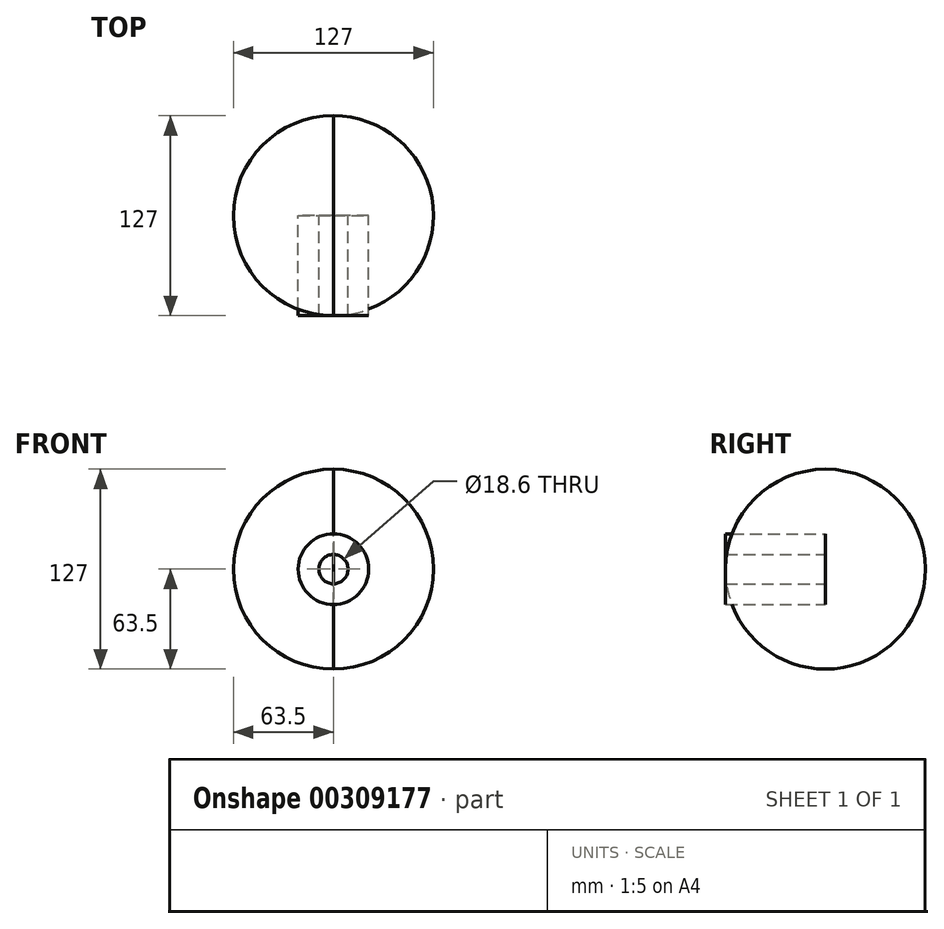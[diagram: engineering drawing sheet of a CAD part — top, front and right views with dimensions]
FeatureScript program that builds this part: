
annotation { "Feature Type Name" : "Feature", "Feature Type Description" : "" }
export const myFeature = defineFeature(function(context is Context, id is Id, definition is map)
    precondition{}
    {
        {
            var Q0;
            Q0=qCreatedBy(makeId("Top.planeOp"),FACE);
            var sketch = newSketch(context, id + "F0", { "sketchPlane" : qUnion([Q0])});
            skCircle(sketch, "E0", {"center": v(0, 0) * mm, "radius": 63.5 * mm});
            skLineSegment(sketch, "E1", {"start": v(0, 63.5) * mm, "end": v(0, -63.5) * mm});
            skSolve(sketch);
        }
        {
            var Q0;
            {var subQ0=sQuery(id+"F0.wireOp",EDGE,"E1");Q0=makeQuery(id+"F0.imprint","IMPRINT",FACE,{"disambiguationData":[TD([[makeQuery(id+"F0.imprint","IMPRINT",EDGE,{"derivedFrom":subQ0}),-1.0]])]});}
            var Q1;
            Q1=sQuery(id+"F0.wireOp",EDGE,"E1");
            revolve(context, id + "F1", {"entities" : qUnion([Q0]), "axis" : qUnion([Q1]), "revolveType" : RevolveType.SYMMETRIC, "angle" : 180 * degree});
        }
        {
            var Q0;
            {var subQ0=sQuery(id+"F0.wireOp",EDGE,"E1");Q0=makeQuery(id+"F0.imprint","IMPRINT",FACE,{"disambiguationData":[TD([[makeQuery(id+"F0.imprint","IMPRINT",EDGE,{"derivedFrom":subQ0}),1.0]])]});}
            var Q1;
            Q1=sQuery(id+"F0.wireOp",EDGE,"E1");
            revolve(context, id + "F2", {"entities" : qUnion([Q0]), "axis" : qUnion([Q1]), "revolveType" : RevolveType.SYMMETRIC, "angle" : 180 * degree});
        }
        {
            var Q0;
            Q0=qCreatedBy(makeId("Front.planeOp"),FACE);
            var sketch = newSketch(context, id + "F3", { "sketchPlane" : qUnion([Q0])});
            skCircle(sketch, "E2", {"center": v(0, 0) * mm, "radius": 22.42 * mm});
            skCircle(sketch, "E3", {"center": v(0, 0) * mm, "radius": 9.3 * mm});
            skSolve(sketch);
        }
        {
            var Q0;
            Q0 = qSketchRegion(id + "F3", true);
            extrude(context, id + "F4", {"entities" : qUnion([Q0]), "depth" : 63.5 * mm});
        }
    });
